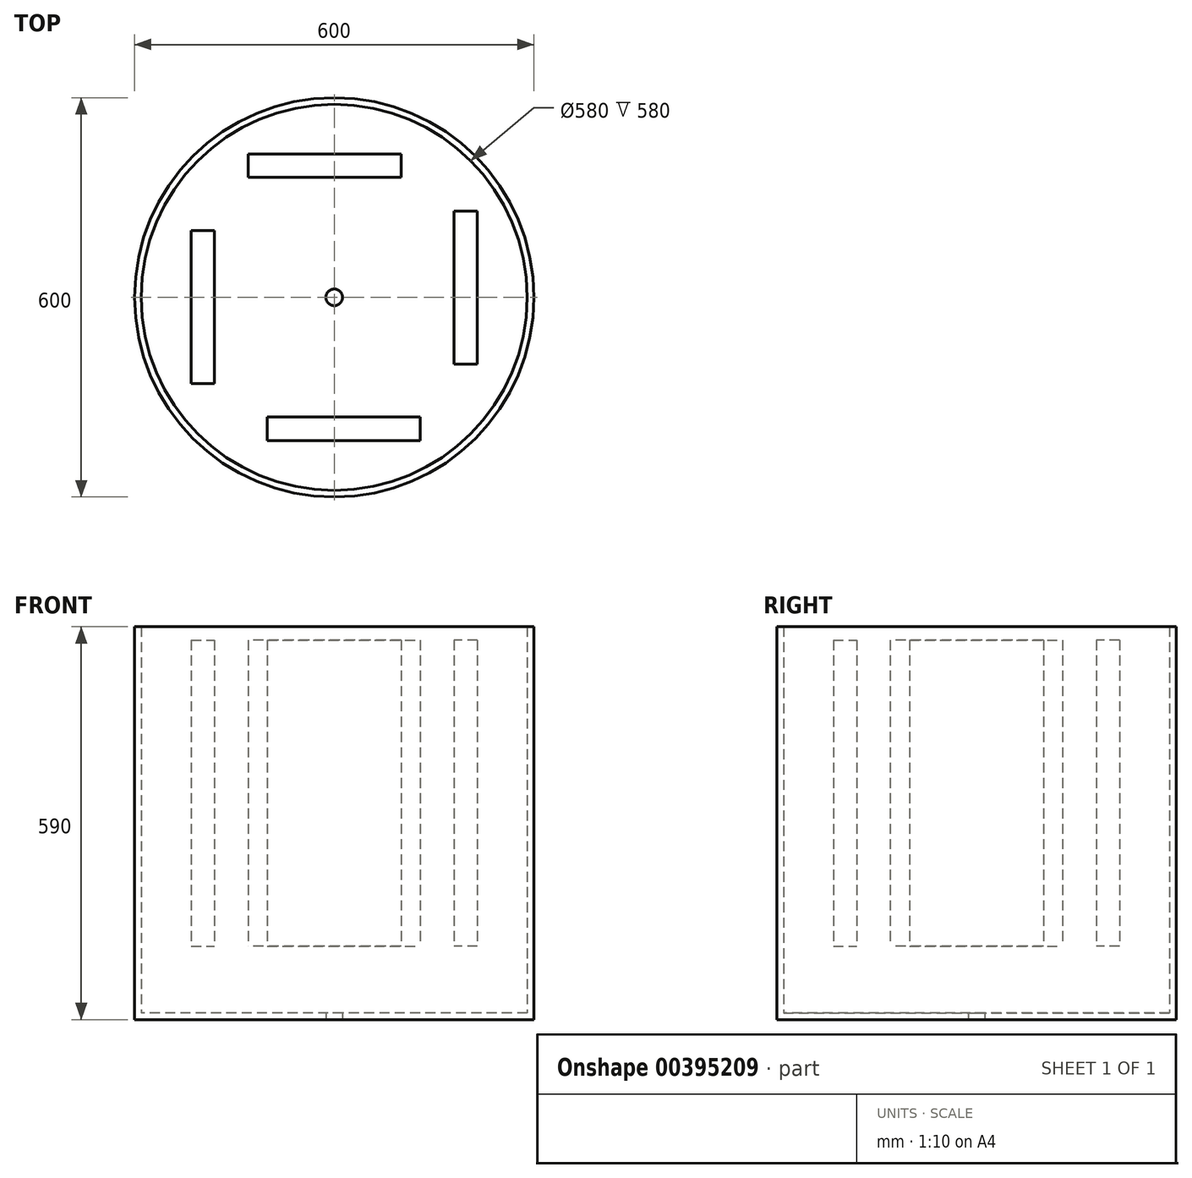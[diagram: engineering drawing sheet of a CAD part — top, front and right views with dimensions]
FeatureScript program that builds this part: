
annotation { "Feature Type Name" : "Feature", "Feature Type Description" : "" }
export const myFeature = defineFeature(function(context is Context, id is Id, definition is map)
    precondition{}
    {
        {
            var Q0;
            Q0=qCreatedBy(makeId("Top.planeOp"),FACE);
            var sketch = newSketch(context, id + "F0", { "sketchPlane" : qUnion([Q0])});
            skCircle(sketch, "E0", {"center": v(0, 0) * mm, "radius": 300 * mm});
            skCircle(sketch, "E1", {"center": v(0, 0) * mm, "radius": 290 * mm});
            skCircle(sketch, "E2", {"center": v(0, 0) * mm, "radius": 12.5 * mm});
            skSolve(sketch);
        }
        {
            var Q0;
            Q0 = qSketchRegion(id + "F0", true);
            var Q1;
            Q1=makeQuery(id+"F0.imprint","IMPRINT",FACE,{"disambiguationData":[TD([[makeQuery(id+"F0.imprint","IMPRINT",EDGE,{"derivedFrom":sQuery(id+"F0.wireOp",EDGE,"E1")}),1.0]])]});
            extrude(context, id + "F1", {"entities" : qUnion([Q0, Q1]), "depth" : 10 * mm});
        }
        {
            var Q0;
            Q0 = qSketchRegion(id + "F0", true);
            extrude(context, id + "F2", {"entities" : qUnion([Q0]), "operationType" : NewBodyOperationType.ADD, "depth" : 590 * mm});
        }
        {
            var Q0;
            Q0=sQuery(id+"F0.wireOp",EDGE,"E2");
            extrude(context, id + "F3", {"bodyType" : ToolBodyType.SURFACE, "surfaceEntities" : qUnion([Q0]), "depth" : 700 * mm});
        }
        {
            var Q0;
            Q0=makeQuery(id+"F1.opExtrude","CAP_FACE",FACE,{"disambiguationData":[OSD([sQuery(id+"F0.wireOp",EDGE,"E0"),sQuery(id+"F0.wireOp",EDGE,"E2")])],"isStart":false});
            var sketch = newSketch(context, id + "F4", { "sketchPlane" : qUnion([Q0])});
            skLineSegment(sketch, "E3.bottom", {"start": v(-215, 100.6) * mm, "end": v(-180, 100.6) * mm});
            skLineSegment(sketch, "E3.top", {"start": v(-215, -129.4) * mm, "end": v(-180, -129.4) * mm});
            skLineSegment(sketch, "E3.left", {"start": v(-215, 100.6) * mm, "end": v(-215, -129.4) * mm});
            skLineSegment(sketch, "E3.right", {"start": v(-180, 100.6) * mm, "end": v(-180, -129.4) * mm});
            skSolve(sketch);
        }
        {
            var Q0;
            Q0=makeQuery(id+"F4.imprint","IMPRINT",FACE,{"disambiguationData":[TD([[makeQuery(id+"F4.imprint","IMPRINT",EDGE,{"derivedFrom":sQuery(id+"F4.wireOp",EDGE,"E3.bottom")}),-1.0]])]});
            extrude(context, id + "F5", {"entities" : qUnion([Q0]), "depth" : 560 * mm, "hasSecondDirection" : true, "secondDirectionOppositeDirection" : true, "secondDirectionDepth" : -100 * mm});
        }
        {
            var Q0;
            Q0=makeQuery(id+"F5.opExtrude","SWEPT_BODY",BODY,{"disambiguationData":[OSD([sQuery(id+"F4.wireOp",EDGE,"E3.bottom"),sQuery(id+"F4.wireOp",EDGE,"E3.top"),sQuery(id+"F4.wireOp",EDGE,"E3.left"),sQuery(id+"F4.wireOp",EDGE,"E3.right")])]});
            var Q1;
            Q1=sQuery(id+"F0.wireOp",EDGE,"E2");
            circularPattern(context, id + "F6", {"entities" : qUnion([Q0]), "axis" : qUnion([Q1]), "angle" : 360 * degree, "instanceCount" : 4, "equalSpace" : true});
        }
    });
